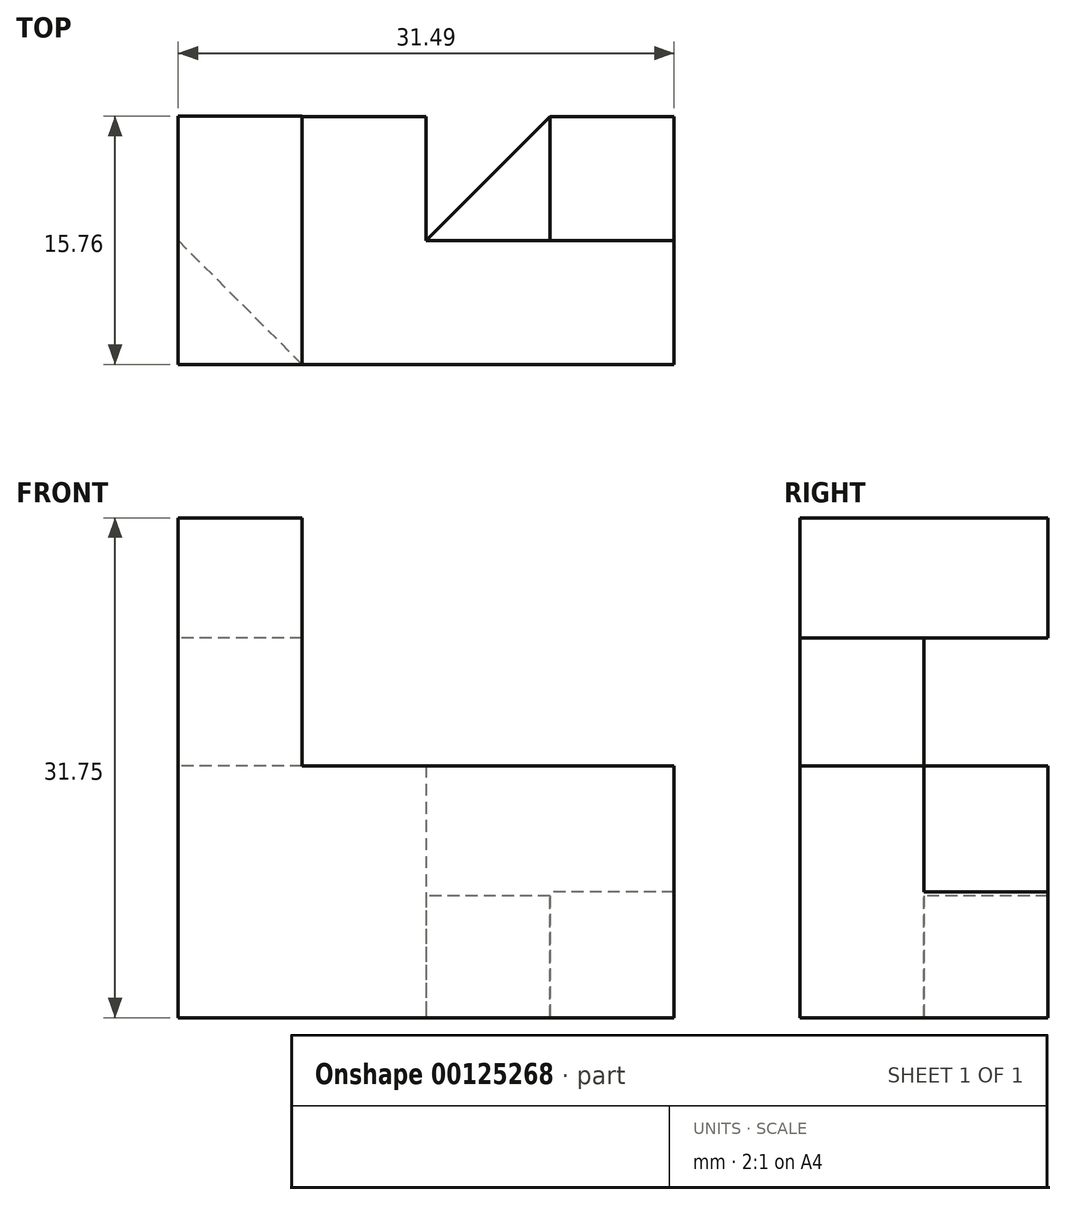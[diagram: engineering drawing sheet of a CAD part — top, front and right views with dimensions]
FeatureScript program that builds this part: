
annotation { "Feature Type Name" : "Feature", "Feature Type Description" : "" }
export const myFeature = defineFeature(function(context is Context, id is Id, definition is map)
    precondition{}
    {
        {
            var Q0;
            Q0=qCreatedBy(makeId("Top.planeOp"),FACE);
            var sketch = newSketch(context, id + "F0", { "sketchPlane" : qUnion([Q0])});
            skLineSegment(sketch, "E0.bottom", {"start": v(7.87, 7.87) * mm, "end": v(-7.87, 7.87) * mm});
            skLineSegment(sketch, "E0.top", {"start": v(7.87, -7.87) * mm, "end": v(-7.87, -7.87) * mm});
            skLineSegment(sketch, "E0.left", {"start": v(7.87, 7.87) * mm, "end": v(7.87, -7.87) * mm});
            skLineSegment(sketch, "E0.right", {"start": v(-7.87, 7.87) * mm, "end": v(-7.87, -7.87) * mm});
            skPoint(sketch, "E0.middle", {"position": v(0, 0) * mm});
            skSolve(sketch);
        }
        {
            var Q0;
            Q0=qSketchRegion(id+"F0",true);
            extrude(context, id + "F1", {"entities" : qUnion([Q0]), "depth" : 16 * mm});
        }
        {
            var Q0;
            Q0=makeQuery(id+"F1.opExtrude","CAP_FACE",FACE,{"disambiguationData":[OSD([sQuery(id+"F0.wireOp",EDGE,"E0.bottom"),sQuery(id+"F0.wireOp",EDGE,"E0.top"),sQuery(id+"F0.wireOp",EDGE,"E0.left"),sQuery(id+"F0.wireOp",EDGE,"E0.right")])],"isStart":false});
            var sketch = newSketch(context, id + "F2", { "sketchPlane" : qUnion([Q0])});
            skLineSegment(sketch, "E1", {"start": v(-7.87, 0) * mm, "end": v(-7.87, -7.87) * mm});
            skLineSegment(sketch, "E2", {"start": v(-7.87, -7.87) * mm, "end": v(0, -7.87) * mm});
            skLineSegment(sketch, "E3", {"start": v(0, -7.87) * mm, "end": v(-7.87, 0) * mm});
            skSolve(sketch);
        }
        {
            var Q0;
            Q0=makeQuery(id+"F2.imprint","IMPRINT",FACE,{"disambiguationData":[TD([[makeQuery(id+"F2.imprint","IMPRINT",EDGE,{"derivedFrom":sQuery(id+"F2.wireOp",EDGE,"E1")}),1.0]])]});
            extrude(context, id + "F3", {"entities" : qUnion([Q0]), "operationType" : NewBodyOperationType.ADD, "depth" : 8.13 * mm});
        }
        {
            var Q0;
            Q0=makeQuery(id+"F3.opExtrude","CAP_FACE",FACE,{"disambiguationData":[OSD([sQuery(id+"F2.wireOp",EDGE,"E1"),sQuery(id+"F2.wireOp",EDGE,"E2"),sQuery(id+"F2.wireOp",EDGE,"E3")])],"isStart":false});
            var sketch = newSketch(context, id + "F4", { "sketchPlane" : qUnion([Q0])});
            skLineSegment(sketch, "E4.bottom", {"start": v(-7.87, -7.87) * mm, "end": v(0, -7.87) * mm});
            skLineSegment(sketch, "E4.top", {"start": v(-7.87, 7.89) * mm, "end": v(0, 7.89) * mm});
            skLineSegment(sketch, "E4.left", {"start": v(-7.87, -7.87) * mm, "end": v(-7.87, 7.89) * mm});
            skLineSegment(sketch, "E4.right", {"start": v(0, -7.87) * mm, "end": v(0, 7.89) * mm});
            skSolve(sketch);
        }
        {
            var Q0;
            {var subQ0=sQuery(id+"F4.wireOp",EDGE,"E4.top");Q0=makeQuery(id+"F4.imprint","IMPRINT",FACE,{"disambiguationData":[TD([[makeQuery(id+"F4.imprint","IMPRINT",EDGE,{"derivedFrom":subQ0}),-1.0]])]});}
            var Q1;
            {var subQ0=sQuery(id+"F4.wireOp",EDGE,"E4.bottom");Q1=makeQuery(id+"F4.imprint","IMPRINT",FACE,{"disambiguationData":[TD([[makeQuery(id+"F4.imprint","IMPRINT",EDGE,{"derivedFrom":subQ0}),-1.0]])]});}
            extrude(context, id + "F5", {"entities" : qUnion([Q0, Q1]), "operationType" : NewBodyOperationType.ADD, "depth" : 7.62 * mm});
        }
        {
            var Q0;
            Q0=makeQuery(id+"F1.opExtrude","SWEPT_FACE",FACE,{"disambiguationData":[OSD([sQuery(id+"F0.wireOp",EDGE,"E0.left")])]});
            var sketch = newSketch(context, id + "F6", { "sketchPlane" : qUnion([Q0])});
            skLineSegment(sketch, "E5.bottom", {"start": v(-7.87, 16) * mm, "end": v(0, 16) * mm});
            skLineSegment(sketch, "E5.top", {"start": v(-7.87, 0) * mm, "end": v(0, 0) * mm});
            skLineSegment(sketch, "E5.left", {"start": v(-7.87, 16) * mm, "end": v(-7.87, 0) * mm});
            skLineSegment(sketch, "E5.right", {"start": v(0, 16) * mm, "end": v(0, 0) * mm});
            skSolve(sketch);
        }
        {
            var Q0;
            Q0=qSketchRegion(id+"F6",true);
            extrude(context, id + "F7", {"entities" : qUnion([Q0]), "operationType" : NewBodyOperationType.ADD, "depth" : 15.75 * mm});
        }
        {
            var Q0;
            Q0=makeQuery(id+"F7.opExtrude","SWEPT_FACE",FACE,{"disambiguationData":[OSD([sQuery(id+"F6.wireOp",EDGE,"E5.right")])]});
            var sketch = newSketch(context, id + "F8", { "sketchPlane" : qUnion([Q0])});
            skLineSegment(sketch, "E6.bottom", {"start": v(-23.62, 0) * mm, "end": v(-15.75, 0) * mm});
            skLineSegment(sketch, "E6.top", {"start": v(-23.62, 7.98) * mm, "end": v(-15.75, 7.98) * mm});
            skLineSegment(sketch, "E6.left", {"start": v(-23.62, 0) * mm, "end": v(-23.62, 7.98) * mm});
            skLineSegment(sketch, "E6.right", {"start": v(-15.75, 0) * mm, "end": v(-15.75, 7.98) * mm});
            skSolve(sketch);
        }
        {
            var Q0;
            Q0=qSketchRegion(id+"F8",true);
            var Q1;
            Q1=makeQuery(id+"F1.opExtrude","SWEPT_FACE",FACE,{"disambiguationData":[OSD([sQuery(id+"F0.wireOp",EDGE,"E0.bottom")])]});
            extrude(context, id + "F9", {"entities" : qUnion([Q0]), "operationType" : NewBodyOperationType.ADD, "endBound" : BoundingType.UP_TO_SURFACE, "endBoundEntityFace" : qUnion([Q1]), "depth" : 25.4 * mm});
        }
        {
            var Q0;
            Q0=makeQuery(id+"F9.boolean.opBoolean","MERGE",FACE,{"derivedFrom":[makeQuery(id+"F7.boolean.opBoolean","MERGE",FACE,{"derivedFrom":[makeQuery(id+"F1.opExtrude","CAP_FACE",FACE,{"disambiguationData":[OSD([sQuery(id+"F0.wireOp",EDGE,"E0.bottom"),sQuery(id+"F0.wireOp",EDGE,"E0.top"),sQuery(id+"F0.wireOp",EDGE,"E0.left"),sQuery(id+"F0.wireOp",EDGE,"E0.right")])],"isStart":true}),makeQuery(id+"F7.opExtrude","SWEPT_FACE",FACE,{"disambiguationData":[OSD([sQuery(id+"F6.wireOp",EDGE,"E5.top")])]})]}),makeQuery(id+"F9.opExtrude","SWEPT_FACE",FACE,{"disambiguationData":[OSD([sQuery(id+"F8.wireOp",EDGE,"E6.bottom")])]})]});
            var sketch = newSketch(context, id + "F10", { "sketchPlane" : qUnion([Q0])});
            skLineSegment(sketch, "E7", {"start": v(15.75, -7.87) * mm, "end": v(7.87, 0) * mm});
            skLineSegment(sketch, "E8", {"start": v(15.75, -7.87) * mm, "end": v(15.75, 0) * mm});
            skLineSegment(sketch, "E9", {"start": v(15.75, 0) * mm, "end": v(7.87, 0) * mm});
            skSolve(sketch);
        }
        {
            var Q0;
            Q0=qSketchRegion(id+"F10",true);
            var Q1;
            Q1=makeQuery(id+"F9.opExtrude","CAP_FACE",FACE,{"disambiguationData":[OSD([sQuery(id+"F0.wireOp",EDGE,"E0.bottom")])],"isStart":false});
            extrude(context, id + "F11", {"entities" : qUnion([Q0]), "oppositeDirection" : true, "endBoundEntityFace" : qUnion([Q1]), "depth" : 7.75 * mm});
        }
    });
